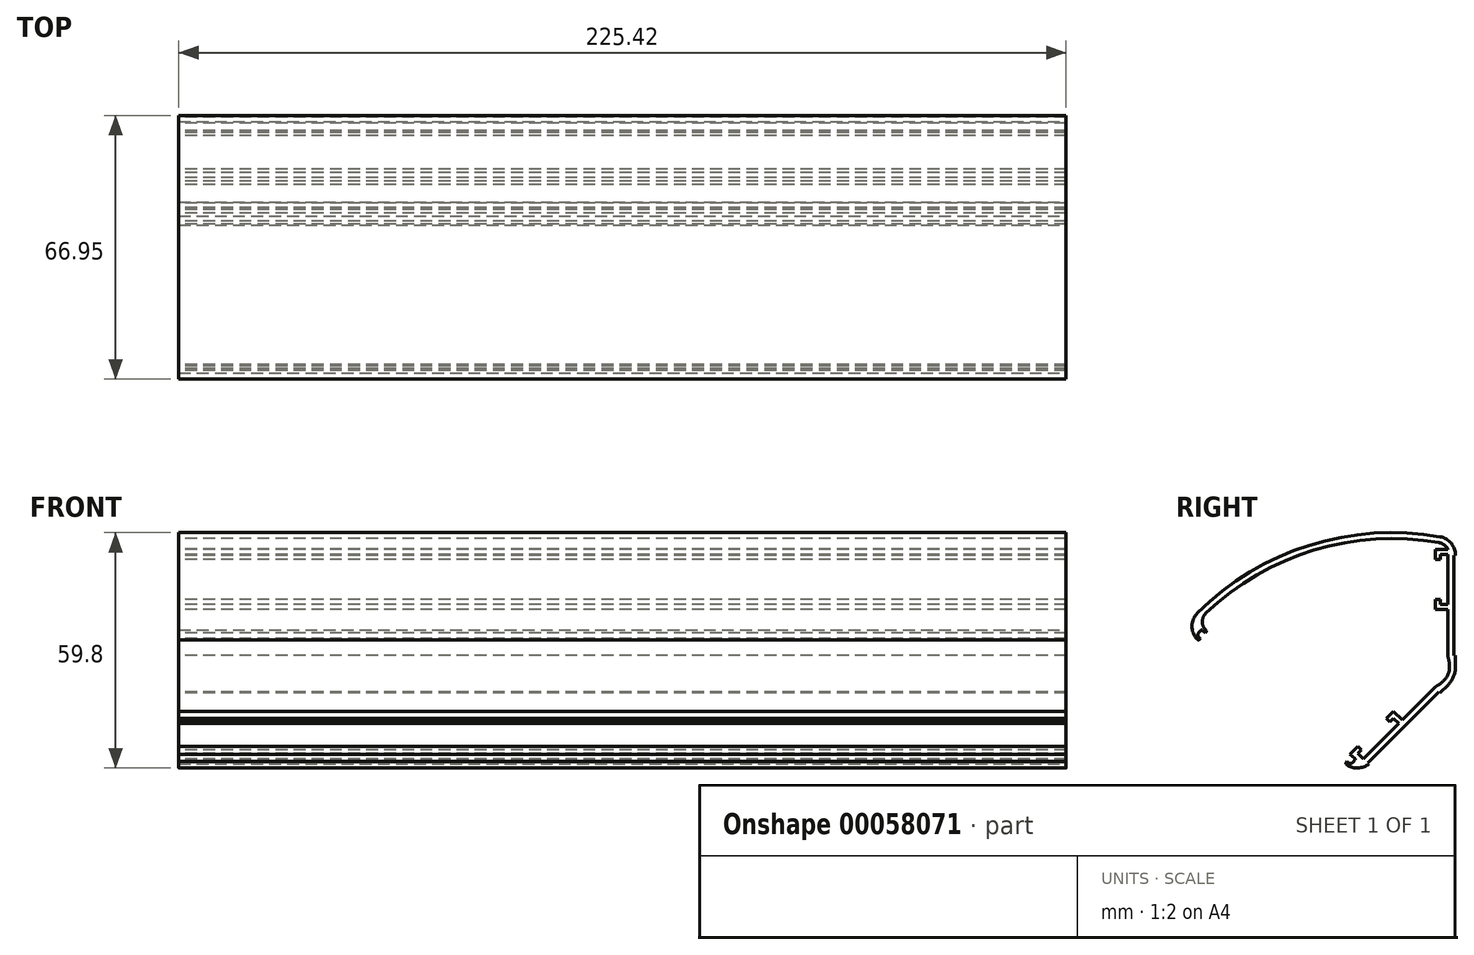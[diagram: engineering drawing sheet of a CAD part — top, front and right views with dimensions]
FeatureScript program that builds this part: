
annotation { "Feature Type Name" : "Feature", "Feature Type Description" : "" }
export const myFeature = defineFeature(function(context is Context, id is Id, definition is map)
    precondition{}
    {
        {
            var Q0;
            Q0=qCreatedBy(makeId("Right.planeOp"),FACE);
            var sketch = newSketch(context, id + "F0", { "sketchPlane" : qUnion([Q0])});
            skLineSegment(sketch, "E0", {"start": v(-24.7, -24.7) * mm, "end": v(0, 0) * mm});
            skLineSegment(sketch, "E1", {"start": v(0, 0) * mm, "end": v(0, 34.93) * mm});
            skArc(sketch, "E2", {"start": v(0, 34.93) * mm, "mid": v(-35.4, 34.1) * mm, "end": v(-65.86, 16.04) * mm});
            skLineSegment(sketch, "E3", {"start": v(-65.86, 16.04) * mm, "end": v(-69.2, 12.66) * mm});
            skLineSegment(sketch, "E4", {"start": v(-24.7, -24.7) * mm, "end": v(-69.2, 12.66) * mm});
            skLineSegment(sketch, "E5", {"start": v(-65.86, 16.04) * mm, "end": v(-24.7, -24.7) * mm, "construction": true});
            skLineSegment(sketch, "E6", {"start": v(-65.86, 16.04) * mm, "end": v(0, 34.93) * mm, "construction": true});
            skSolve(sketch);
        }
        {
            var Q0;
            Q0=qSketchRegion(id+"F0",true);
            extrude(context, id + "F1", {"entities" : qUnion([Q0]), "endBound" : BoundingType.SYMMETRIC, "depth" : 225.42 * mm});
        }
        {
            var Q0;
            Q0=makeQuery(id+"F1.opExtrude","SWEPT_EDGE",EDGE,{"disambiguationData":[OSD([sQuery(id+"F0.wireOp",EDGE,"E1"),sQuery(id+"F0.wireOp",EDGE,"E2")])]});
            var Q1;
            Q1=makeQuery(id+"F1.opExtrude","SWEPT_EDGE",EDGE,{"disambiguationData":[OSD([sQuery(id+"F0.wireOp",EDGE,"E0"),sQuery(id+"F0.wireOp",EDGE,"E4")])]});
            var Q2;
            Q2=makeQuery(id+"F1.opExtrude","SWEPT_EDGE",EDGE,{"disambiguationData":[OSD([sQuery(id+"F0.wireOp",EDGE,"E3"),sQuery(id+"F0.wireOp",EDGE,"E4")])]});
            fillet(context, id + "F2", {"entities" : qUnion([Q0, Q1, Q2]), "radius" : 4.76 * mm, "tangentPropagation" : true, "allowEdgeOverflow" : false});
        }
        {
            var Q0;
            Q0=makeQuery(id+"F1.opExtrude","SWEPT_EDGE",EDGE,{"disambiguationData":[OSD([sQuery(id+"F0.wireOp",EDGE,"E0"),sQuery(id+"F0.wireOp",EDGE,"E1")])]});
            fillet(context, id + "F3", {"entities" : qUnion([Q0]), "radius" : 6.35 * mm, "tangentPropagation" : true, "allowEdgeOverflow" : false});
        }
        {
            var Q0;
            Q0=makeQuery(id+"F1.opExtrude","CAP_FACE",FACE,{"disambiguationData":[OSD([sQuery(id+"F0.wireOp",EDGE,"E0"),sQuery(id+"F0.wireOp",EDGE,"E1"),sQuery(id+"F0.wireOp",EDGE,"E2"),sQuery(id+"F0.wireOp",EDGE,"E3"),sQuery(id+"F0.wireOp",EDGE,"E4")])],"isStart":true});
            var Q1;
            Q1=makeQuery(id+"F1.opExtrude","CAP_FACE",FACE,{"disambiguationData":[OSD([sQuery(id+"F0.wireOp",EDGE,"E0"),sQuery(id+"F0.wireOp",EDGE,"E1"),sQuery(id+"F0.wireOp",EDGE,"E2"),sQuery(id+"F0.wireOp",EDGE,"E3"),sQuery(id+"F0.wireOp",EDGE,"E4")])],"isStart":false});
            var Q2;
            Q2=makeQuery(id+"F1.opExtrude","SWEPT_FACE",FACE,{"disambiguationData":[OSD([sQuery(id+"F0.wireOp",EDGE,"E4")])]});
            shell(context, id + "F4", {"entities" : qUnion([Q0, Q1, Q2]), "thickness" : 1.52 * mm});
        }
        {
            var Q0;
            Q0=makeQuery(id+"F1.opExtrude","CAP_FACE",FACE,{"disambiguationData":[OSD([sQuery(id+"F0.wireOp",EDGE,"E0"),sQuery(id+"F0.wireOp",EDGE,"E1"),sQuery(id+"F0.wireOp",EDGE,"E2"),sQuery(id+"F0.wireOp",EDGE,"E3"),sQuery(id+"F0.wireOp",EDGE,"E4")])],"isStart":true});
            var sketch = newSketch(context, id + "F5", { "sketchPlane" : qUnion([Q0])});
            skLineSegment(sketch, "E7", {"start": v(64.27, 10.5) * mm, "end": v(63.2, 11.76) * mm});
            skArc(sketch, "E8.0", {"start": v(64.27, 10.5) * mm, "mid": v(65.42, 12.84) * mm, "end": v(64.47, 15.27) * mm});
            skArc(sketch, "E9", {"start": v(63.2, 11.76) * mm, "mid": v(64.32, 14.02) * mm, "end": v(63.37, 16.35) * mm});
            skSolve(sketch);
        }
        {
            var Q0;
            {var subQ0=sQuery(id+"F0.wireOp",EDGE,"E3");Q0=makeQuery(id+"FXWxfeTe23RxrKB_1.boolean.opBoolean","MERGE",FACE,{"derivedFrom":[makeQuery(id+"F1.opExtrude","CAP_FACE",FACE,{"disambiguationData":[OSD([sQuery(id+"F0.wireOp",EDGE,"E0"),sQuery(id+"F0.wireOp",EDGE,"E1"),sQuery(id+"F0.wireOp",EDGE,"E2"),subQ0,sQuery(id+"F0.wireOp",EDGE,"E4")])],"isStart":true}),makeQuery(id+"FXWxfeTe23RxrKB_1.opExtrude","CAP_FACE",FACE,{"disambiguationData":[OSD([subQ0,sQuery(id+"F5.wireOp",EDGE,"f8929549-29da-4568-b1ae-587f62ae2228.0"),sQuery(id+"F5.wireOp",EDGE,"E7"),sQuery(id+"F5.wireOp",EDGE,"b0cd2a88-d953-423b-8e6f-4eb86873c5e2")])],"isStart":true})]});}
            var sketch = newSketch(context, id + "F6", { "sketchPlane" : qUnion([Q0])});
            skArc(sketch, "E10.0", {"start": v(22.69, -20.53) * mm, "mid": v(24.84, -21.48) * mm, "end": v(27.06, -20.72) * mm});
            skLineSegment(sketch, "E11", {"start": v(27.06, -20.72) * mm, "end": v(26, -19.46) * mm});
            skArc(sketch, "E12", {"start": v(21.41, -19.26) * mm, "mid": v(23.67, -20.25) * mm, "end": v(26, -19.46) * mm});
            skLineSegment(sketch, "E13", {"start": v(26, -19.46) * mm, "end": v(23.84, -21.27) * mm, "construction": true});
            skSolve(sketch);
        }
        {
            var Q0;
            Q0=makeQuery(id+"F5.imprint","IMPRINT",FACE,{"disambiguationData":[TD([[makeQuery(id+"F5.imprint","IMPRINT",EDGE,{"derivedFrom":sQuery(id+"F5.wireOp",EDGE,"E7")}),-1.0]])]});
            var Q1;
            {var subQ0=sQuery(id+"F6.wireOp",EDGE,"E10.0");Q1=makeQuery(id+"F6.imprint","IMPRINT",FACE,{"disambiguationData":[TD([[makeQuery(id+"F6.imprint","IMPRINT",EDGE,{"derivedFrom":subQ0}),1.0]])]});}
            var Q2;
            Q2=makeQuery(id+"F1.opExtrude","CAP_FACE",FACE,{"disambiguationData":[OSD([sQuery(id+"F0.wireOp",EDGE,"E0"),sQuery(id+"F0.wireOp",EDGE,"E1"),sQuery(id+"F0.wireOp",EDGE,"E2"),sQuery(id+"F0.wireOp",EDGE,"E3"),sQuery(id+"F0.wireOp",EDGE,"E4")])],"isStart":false});
            extrude(context, id + "F7", {"entities" : qUnion([Q0, Q1]), "operationType" : NewBodyOperationType.ADD, "endBound" : BoundingType.UP_TO_SURFACE, "oppositeDirection" : true, "endBoundEntityFace" : qUnion([Q2]), "depth" : 25.4 * mm});
        }
        {
            var Q0;
            {var subQ0=sQuery(id+"F0.wireOp",EDGE,"E0");var subQ1=sQuery(id+"F0.wireOp",EDGE,"E2");Q0=makeQuery(id+"F7.boolean.opBoolean","MERGE",FACE,{"derivedFrom":[makeQuery(id+"F1.opExtrude","CAP_FACE",FACE,{"disambiguationData":[OSD([subQ0,sQuery(id+"F0.wireOp",EDGE,"E1"),subQ1,sQuery(id+"F0.wireOp",EDGE,"E3"),sQuery(id+"F0.wireOp",EDGE,"E4")])],"isStart":true}),makeQuery(id+"F7.opExtrude","CAP_FACE",FACE,{"disambiguationData":[OSD([subQ1,sQuery(id+"F5.wireOp",EDGE,"E7"),sQuery(id+"F5.wireOp",EDGE,"E8.0"),sQuery(id+"F5.wireOp",EDGE,"E9")])],"isStart":true}),makeQuery(id+"F7.opExtrude","CAP_FACE",FACE,{"disambiguationData":[OSD([subQ0,sQuery(id+"F6.wireOp",EDGE,"E10.0"),sQuery(id+"F6.wireOp",EDGE,"E11"),sQuery(id+"F6.wireOp",EDGE,"E12")])],"isStart":true})]});}
            var sketch = newSketch(context, id + "F8", { "sketchPlane" : qUnion([Q0])});
            skLineSegment(sketch, "E14", {"start": v(64.19, 10.6) * mm, "end": v(26.98, -20.63) * mm, "construction": true});
            skSolve(sketch);
        }
        {
            var Q0;
            {var subQ4=sQuery(id+"F0.wireOp",EDGE,"E0");var subQ12=makeQuery(id+"F1.opExtrude","CAP_EDGE",EDGE,{"disambiguationData":[OSD([subQ4])],"isStart":true});Q0=makeQuery(id+"F8.imprint","IMPRINT",FACE,{"disambiguationData":[TD([[makeQuery(id+"F8.imprint","IMPRINT",EDGE,{"derivedFrom":subQ12}),-1.0]])]});}
            var sketch = newSketch(context, id + "F9", { "sketchPlane" : qUnion([Q0])});
            skLineSegment(sketch, "E15", {"start": v(63.57, 11.33) * mm, "end": v(64.8, 9.87) * mm});
            skLineSegment(sketch, "E16", {"start": v(64.8, 9.87) * mm, "end": v(65.77, 10.68) * mm});
            skLineSegment(sketch, "E17", {"start": v(65.77, 10.68) * mm, "end": v(64.55, 12.14) * mm});
            skLineSegment(sketch, "E18", {"start": v(64.55, 12.14) * mm, "end": v(63.57, 11.33) * mm});
            skPoint(sketch, "E19", {"position": v(64.19, 10.6) * mm});
            skSolve(sketch);
        }
        {
            var Q0;
            {var subQ4=sQuery(id+"F0.wireOp",EDGE,"E0");var subQ12=makeQuery(id+"F1.opExtrude","CAP_EDGE",EDGE,{"disambiguationData":[OSD([subQ4])],"isStart":true});Q0=makeQuery(id+"F8.imprint","IMPRINT",FACE,{"disambiguationData":[TD([[makeQuery(id+"F8.imprint","IMPRINT",EDGE,{"derivedFrom":subQ12}),-1.0]])]});}
            var sketch = newSketch(context, id + "F10", { "sketchPlane" : qUnion([Q0])});
            skLineSegment(sketch, "E20", {"start": v(26.37, -19.9) * mm, "end": v(27.59, -21.36) * mm});
            skLineSegment(sketch, "E21", {"start": v(27.59, -21.36) * mm, "end": v(26.62, -22.17) * mm});
            skLineSegment(sketch, "E22", {"start": v(26.62, -22.17) * mm, "end": v(25.4, -20.71) * mm});
            skLineSegment(sketch, "E23", {"start": v(25.4, -20.71) * mm, "end": v(26.37, -19.9) * mm});
            skPoint(sketch, "E24", {"position": v(26.98, -20.63) * mm});
            skSolve(sketch);
        }
        {
            var Q0;
            Q0=qSketchRegion(id+"F9",true);
            var Q1;
            Q1=qSketchRegion(id+"F10",true);
            var Q2;
            {var subQ0=sQuery(id+"F0.wireOp",EDGE,"E0");var subQ1=sQuery(id+"F0.wireOp",EDGE,"E2");Q2=makeQuery(id+"F7.boolean.opBoolean","MERGE",FACE,{"derivedFrom":[makeQuery(id+"F1.opExtrude","CAP_FACE",FACE,{"disambiguationData":[OSD([subQ0,sQuery(id+"F0.wireOp",EDGE,"E1"),subQ1,sQuery(id+"F0.wireOp",EDGE,"E3"),sQuery(id+"F0.wireOp",EDGE,"E4")])],"isStart":false}),makeQuery(id+"F7.opExtrude","CAP_FACE",FACE,{"disambiguationData":[OSD([subQ1,sQuery(id+"F5.wireOp",EDGE,"E7"),sQuery(id+"F5.wireOp",EDGE,"E8.0"),sQuery(id+"F5.wireOp",EDGE,"E9")])],"isStart":false}),makeQuery(id+"F7.opExtrude","CAP_FACE",FACE,{"disambiguationData":[OSD([subQ0,sQuery(id+"F6.wireOp",EDGE,"E10.0"),sQuery(id+"F6.wireOp",EDGE,"E11"),sQuery(id+"F6.wireOp",EDGE,"E12")])],"isStart":false})]});}
            extrude(context, id + "F11", {"entities" : qUnion([Q0, Q1]), "operationType" : NewBodyOperationType.REMOVE, "endBound" : BoundingType.UP_TO_SURFACE, "oppositeDirection" : true, "endBoundEntityFace" : qUnion([Q2]), "depth" : 25.4 * mm});
        }
        {
            var Q0;
            Q0=makeQuery(id+"F11.boolean.opBoolean","COPY",EDGE,{"derivedFrom":makeQuery(id+"F11.opExtrude","SWEPT_EDGE",EDGE,{"disambiguationData":[OSD([sQuery(id+"F10.wireOp",EDGE,"E21"),sQuery(id+"F10.wireOp",EDGE,"E22")])]})});
            var Q1;
            Q1=makeQuery(id+"F11.boolean.opBoolean","COPY",EDGE,{"derivedFrom":makeQuery(id+"F11.opExtrude","SWEPT_EDGE",EDGE,{"disambiguationData":[OSD([sQuery(id+"F9.wireOp",EDGE,"E16"),sQuery(id+"F9.wireOp",EDGE,"E17")])]})});
            fillet(context, id + "F12", {"entities" : qUnion([Q0, Q1]), "radius" : 0.76 * mm, "tangentPropagation" : true, "allowEdgeOverflow" : false});
        }
        {
            var Q0;
            {var subQ0=sQuery(id+"F0.wireOp",EDGE,"E4");Q0=makeQuery(id+"F2.opFillet","BLEND_EDGE",EDGE,{"blendedFrom":[makeQuery(id+"F1.opExtrude","SWEPT_EDGE",EDGE,{"disambiguationData":[OSD([sQuery(id+"F0.wireOp",EDGE,"E3"),subQ0])]}),makeQuery(id+"F1.opExtrude","SWEPT_FACE",FACE,{"disambiguationData":[OSD([subQ0])]})],"blendedInto":[makeQuery(id+"F1.opExtrude","SWEPT_FACE",FACE,{"disambiguationData":[OSD([subQ0])]})]});}
            var Q1;
            {var subQ0=sQuery(id+"F0.wireOp",EDGE,"E4");Q1=makeQuery(id+"F2.opFillet","BLEND_EDGE",EDGE,{"blendedFrom":[makeQuery(id+"F1.opExtrude","SWEPT_EDGE",EDGE,{"disambiguationData":[OSD([sQuery(id+"F0.wireOp",EDGE,"E0"),subQ0])]}),makeQuery(id+"F1.opExtrude","SWEPT_FACE",FACE,{"disambiguationData":[OSD([subQ0])]})],"blendedInto":[makeQuery(id+"F1.opExtrude","SWEPT_FACE",FACE,{"disambiguationData":[OSD([subQ0])]})]});}
            fillet(context, id + "F13", {"entities" : qUnion([Q0, Q1]), "radius" : 0.5 * mm, "tangentPropagation" : true, "allowEdgeOverflow" : false});
        }
        {
            var Q0;
            Q0=makeQuery(id+"F11.boolean.opBoolean","COPY",EDGE,{"derivedFrom":makeQuery(id+"F11.opExtrude","SWEPT_EDGE",EDGE,{"disambiguationData":[OSD([sQuery(id+"F10.wireOp",EDGE,"E22"),sQuery(id+"F10.wireOp",EDGE,"E23")])]})});
            var Q1;
            Q1=makeQuery(id+"F11.boolean.opBoolean","COPY",EDGE,{"derivedFrom":makeQuery(id+"F11.opExtrude","SWEPT_EDGE",EDGE,{"disambiguationData":[OSD([sQuery(id+"F0.wireOp",EDGE,"E0"),sQuery(id+"F0.wireOp",EDGE,"E1"),sQuery(id+"F0.wireOp",EDGE,"E2"),sQuery(id+"F0.wireOp",EDGE,"E3"),sQuery(id+"F0.wireOp",EDGE,"E4"),sQuery(id+"F6.wireOp",EDGE,"E11"),sQuery(id+"F10.wireOp",EDGE,"E20"),sQuery(id+"F10.wireOp",EDGE,"E23")])]})});
            var Q2;
            Q2=makeQuery(id+"F7.opExtrude","SWEPT_EDGE",EDGE,{"disambiguationData":[OSD([sQuery(id+"F6.wireOp",EDGE,"E11"),sQuery(id+"F6.wireOp",EDGE,"E12")])]});
            var Q3;
            Q3=makeQuery(id+"F11.boolean.opBoolean","COPY",EDGE,{"derivedFrom":makeQuery(id+"F11.opExtrude","SWEPT_EDGE",EDGE,{"disambiguationData":[OSD([sQuery(id+"F0.wireOp",EDGE,"E0"),sQuery(id+"F0.wireOp",EDGE,"E1"),sQuery(id+"F0.wireOp",EDGE,"E2"),sQuery(id+"F0.wireOp",EDGE,"E3"),sQuery(id+"F0.wireOp",EDGE,"E4"),sQuery(id+"F5.wireOp",EDGE,"E7"),sQuery(id+"F9.wireOp",EDGE,"E15"),sQuery(id+"F9.wireOp",EDGE,"E18")])]})});
            var Q4;
            Q4=makeQuery(id+"F7.opExtrude","SWEPT_EDGE",EDGE,{"disambiguationData":[OSD([sQuery(id+"F5.wireOp",EDGE,"E7"),sQuery(id+"F5.wireOp",EDGE,"E9")])]});
            var Q5;
            Q5=makeQuery(id+"F11.boolean.opBoolean","COPY",EDGE,{"derivedFrom":makeQuery(id+"F11.opExtrude","SWEPT_EDGE",EDGE,{"disambiguationData":[OSD([sQuery(id+"F9.wireOp",EDGE,"E17"),sQuery(id+"F9.wireOp",EDGE,"E18")])]})});
            fillet(context, id + "F14", {"entities" : qUnion([Q0, Q1, Q2, Q3, Q4, Q5]), "radius" : 0.25 * mm, "tangentPropagation" : true, "allowEdgeOverflow" : false});
        }
        {
            var Q0;
            {var subQ2=sQuery(id+"F0.wireOp",EDGE,"E2");var subQ10=makeQuery(id+"F1.opExtrude","CAP_EDGE",EDGE,{"disambiguationData":[OSD([subQ2])],"isStart":true});Q0=makeQuery(id+"F8.imprint","IMPRINT",FACE,{"disambiguationData":[TD([[makeQuery(id+"F8.imprint","IMPRINT",EDGE,{"derivedFrom":subQ10}),-1.0]])]});}
            var sketch = newSketch(context, id + "F15", { "sketchPlane" : qUnion([Q0])});
            skLineSegment(sketch, "E25.0", {"start": v(0, 0) * mm, "end": v(0, 31.05) * mm, "construction": true});
            skLineSegment(sketch, "E25.1", {"start": v(21.6, -21.6) * mm, "end": v(0, 0) * mm, "construction": true});
            skLineSegment(sketch, "E26", {"start": v(0, 0) * mm, "end": v(1.9, 0.78) * mm, "construction": true});
            skSolve(sketch);
        }
        {
            var Q0;
            {var subQ2=sQuery(id+"F0.wireOp",EDGE,"E2");var subQ10=makeQuery(id+"F1.opExtrude","CAP_EDGE",EDGE,{"disambiguationData":[OSD([subQ2])],"isStart":true});Q0=makeQuery(id+"F8.imprint","IMPRINT",FACE,{"disambiguationData":[TD([[makeQuery(id+"F8.imprint","IMPRINT",EDGE,{"derivedFrom":subQ10}),-1.0]])]});}
            var sketch = newSketch(context, id + "F16", { "sketchPlane" : qUnion([Q0])});
            skLineSegment(sketch, "E27.bottom", {"start": v(0, 31.05) * mm, "end": v(0.4, 31.05) * mm});
            skLineSegment(sketch, "E27.top", {"start": v(0, 5.65) * mm, "end": v(0.4, 5.65) * mm});
            skLineSegment(sketch, "E27.left", {"start": v(0, 31.05) * mm, "end": v(0, 5.65) * mm});
            skLineSegment(sketch, "E27.right", {"start": v(0.4, 31.05) * mm, "end": v(0.4, 5.65) * mm});
            skLineSegment(sketch, "E28.MirrorCS", {"start": v(4, -4) * mm, "end": v(4.27, -3.71) * mm});
            skLineSegment(sketch, "E29.MirrorCS", {"start": v(22.23, -21.67) * mm, "end": v(4.27, -3.71) * mm});
            skLineSegment(sketch, "E30.MirrorCS", {"start": v(21.95, -21.95) * mm, "end": v(4, -4) * mm});
            skLineSegment(sketch, "E31.MirrorCS", {"start": v(21.95, -21.95) * mm, "end": v(22.23, -21.67) * mm});
            skSolve(sketch);
        }
        {
            var Q0;
            Q0=qSketchRegion(id+"F16",true);
            var Q1;
            {var subQ0=sQuery(id+"F0.wireOp",EDGE,"E0");var subQ1=sQuery(id+"F0.wireOp",EDGE,"E2");Q1=makeQuery(id+"F7.boolean.opBoolean","MERGE",FACE,{"derivedFrom":[makeQuery(id+"F1.opExtrude","CAP_FACE",FACE,{"disambiguationData":[OSD([subQ0,sQuery(id+"F0.wireOp",EDGE,"E1"),subQ1,sQuery(id+"F0.wireOp",EDGE,"E3"),sQuery(id+"F0.wireOp",EDGE,"E4")])],"isStart":false}),makeQuery(id+"F7.opExtrude","CAP_FACE",FACE,{"disambiguationData":[OSD([subQ1,sQuery(id+"F5.wireOp",EDGE,"E7"),sQuery(id+"F5.wireOp",EDGE,"E8.0"),sQuery(id+"F5.wireOp",EDGE,"E9")])],"isStart":false}),makeQuery(id+"F7.opExtrude","CAP_FACE",FACE,{"disambiguationData":[OSD([subQ0,sQuery(id+"F6.wireOp",EDGE,"E10.0"),sQuery(id+"F6.wireOp",EDGE,"E11"),sQuery(id+"F6.wireOp",EDGE,"E12")])],"isStart":false})]});}
            extrude(context, id + "F17", {"entities" : qUnion([Q0]), "operationType" : NewBodyOperationType.REMOVE, "endBound" : BoundingType.UP_TO_SURFACE, "oppositeDirection" : true, "endBoundEntityFace" : qUnion([Q1]), "depth" : 25.4 * mm});
        }
        {
            var Q0;
            {var subQ2=sQuery(id+"F0.wireOp",EDGE,"E2");var subQ10=makeQuery(id+"F1.opExtrude","CAP_EDGE",EDGE,{"disambiguationData":[OSD([subQ2])],"isStart":true});Q0=makeQuery(id+"F8.imprint","IMPRINT",FACE,{"disambiguationData":[TD([[makeQuery(id+"F8.imprint","IMPRINT",EDGE,{"derivedFrom":subQ10}),-1.0]])]});}
            var sketch = newSketch(context, id + "F18", { "sketchPlane" : qUnion([Q0])});
            skLineSegment(sketch, "E32.left", {"start": v(1.52, 31.05) * mm, "end": v(1.52, 2.63) * mm});
            skLineSegment(sketch, "E32.right", {"start": v(1.92, 32.6) * mm, "end": v(1.92, 5.65) * mm});
            skArc(sketch, "E33", {"start": v(1.52, 31.05) * mm, "mid": v(1.62, 31.85) * mm, "end": v(1.92, 32.6) * mm});
            skArc(sketch, "E34", {"start": v(1.92, 5.65) * mm, "mid": v(1.9, 5.25) * mm, "end": v(1.82, 4.85) * mm});
            skArc(sketch, "E35", {"start": v(1.82, 4.85) * mm, "mid": v(1.6, 3.75) * mm, "end": v(1.52, 2.63) * mm});
            skLineSegment(sketch, "E36.MirrorCS", {"start": v(24.4, -21.7) * mm, "end": v(5.35, -2.63) * mm});
            skLineSegment(sketch, "E37.MirrorCS", {"start": v(23.03, -20.88) * mm, "end": v(2.94, -0.78) * mm});
            skArc(sketch, "E38.MirrorCS", {"start": v(4.72, -2.15) * mm, "mid": v(3.78, -1.52) * mm, "end": v(2.94, -0.78) * mm});
            skArc(sketch, "E39.MirrorCS", {"start": v(5.35, -2.63) * mm, "mid": v(5.05, -2.37) * mm, "end": v(4.72, -2.15) * mm});
            skArc(sketch, "E40.MirrorCS", {"start": v(23.03, -20.88) * mm, "mid": v(23.67, -21.37) * mm, "end": v(24.4, -21.7) * mm});
            skSolve(sketch);
        }
        {
            var Q0;
            Q0=qSketchRegion(id+"F18",true);
            var Q1;
            {var subQ0=sQuery(id+"F0.wireOp",EDGE,"E0");var subQ1=sQuery(id+"F0.wireOp",EDGE,"E2");Q1=makeQuery(id+"F7.boolean.opBoolean","MERGE",FACE,{"derivedFrom":[makeQuery(id+"F1.opExtrude","CAP_FACE",FACE,{"disambiguationData":[OSD([subQ0,sQuery(id+"F0.wireOp",EDGE,"E1"),subQ1,sQuery(id+"F0.wireOp",EDGE,"E3"),sQuery(id+"F0.wireOp",EDGE,"E4")])],"isStart":false}),makeQuery(id+"F7.opExtrude","CAP_FACE",FACE,{"disambiguationData":[OSD([subQ1,sQuery(id+"F5.wireOp",EDGE,"E7"),sQuery(id+"F5.wireOp",EDGE,"E8.0"),sQuery(id+"F5.wireOp",EDGE,"E9")])],"isStart":false}),makeQuery(id+"F7.opExtrude","CAP_FACE",FACE,{"disambiguationData":[OSD([subQ0,sQuery(id+"F6.wireOp",EDGE,"E10.0"),sQuery(id+"F6.wireOp",EDGE,"E11"),sQuery(id+"F6.wireOp",EDGE,"E12")])],"isStart":false})]});}
            extrude(context, id + "F19", {"entities" : qUnion([Q0]), "operationType" : NewBodyOperationType.ADD, "endBound" : BoundingType.UP_TO_SURFACE, "oppositeDirection" : true, "endBoundEntityFace" : qUnion([Q1]), "depth" : 25.4 * mm});
        }
        {
            var Q0;
            {var subQ2=sQuery(id+"F0.wireOp",EDGE,"E2");var subQ10=makeQuery(id+"F1.opExtrude","CAP_EDGE",EDGE,{"disambiguationData":[OSD([subQ2])],"isStart":true});Q0=makeQuery(id+"F8.imprint","IMPRINT",FACE,{"disambiguationData":[TD([[makeQuery(id+"F8.imprint","IMPRINT",EDGE,{"derivedFrom":subQ10}),-1.0]])]});}
            var sketch = newSketch(context, id + "F20", { "sketchPlane" : qUnion([Q0])});
            skLineSegment(sketch, "E41", {"start": v(13.55, -10.83) * mm, "end": v(15.8, -8.59) * mm});
            skLineSegment(sketch, "E42", {"start": v(17.59, -10.38) * mm, "end": v(15.8, -8.59) * mm});
            skLineSegment(sketch, "E43", {"start": v(17.59, -10.38) * mm, "end": v(16.7, -11.28) * mm});
            skLineSegment(sketch, "E44", {"start": v(15.8, -10.38) * mm, "end": v(16.7, -11.28) * mm});
            skLineSegment(sketch, "E45", {"start": v(15.8, -10.38) * mm, "end": v(14.45, -11.73) * mm});
            skLineSegment(sketch, "E46", {"start": v(13.55, -10.83) * mm, "end": v(14.45, -11.73) * mm});
            skLineSegment(sketch, "E47", {"start": v(24.77, -17.57) * mm, "end": v(26.77, -19.56) * mm});
            skLineSegment(sketch, "E48", {"start": v(26.77, -19.56) * mm, "end": v(24.32, -21.6) * mm});
            skLineSegment(sketch, "E49", {"start": v(24.32, -21.6) * mm, "end": v(23.43, -20.71) * mm});
            skLineSegment(sketch, "E50", {"start": v(24.77, -17.57) * mm, "end": v(23.88, -18.47) * mm});
            skLineSegment(sketch, "E51", {"start": v(23.88, -18.47) * mm, "end": v(24.77, -19.36) * mm});
            skLineSegment(sketch, "E52", {"start": v(24.77, -19.36) * mm, "end": v(23.43, -20.71) * mm});
            skLineSegment(sketch, "E53.MirrorCS", {"start": v(1.92, 17.24) * mm, "end": v(1.92, 18.5) * mm});
            skLineSegment(sketch, "E54.MirrorCS", {"start": v(1.92, 17.24) * mm, "end": v(5.1, 17.24) * mm});
            skLineSegment(sketch, "E55.MirrorCS", {"start": v(3.83, 18.5) * mm, "end": v(1.92, 18.5) * mm});
            skLineSegment(sketch, "E56.MirrorCS", {"start": v(3.83, 18.5) * mm, "end": v(3.83, 19.78) * mm});
            skLineSegment(sketch, "E57.MirrorCS", {"start": v(5.1, 19.78) * mm, "end": v(3.83, 19.78) * mm});
            skLineSegment(sketch, "E58.MirrorCS", {"start": v(5.1, 19.78) * mm, "end": v(5.1, 17.24) * mm});
            skLineSegment(sketch, "E59.MirrorCS", {"start": v(3.83, 31.2) * mm, "end": v(1.92, 31.2) * mm});
            skLineSegment(sketch, "E60.MirrorCS", {"start": v(3.83, 29.94) * mm, "end": v(3.83, 31.2) * mm});
            skLineSegment(sketch, "E61.MirrorCS", {"start": v(5.1, 29.94) * mm, "end": v(3.83, 29.94) * mm});
            skLineSegment(sketch, "E62.MirrorCS", {"start": v(5.1, 29.94) * mm, "end": v(5.1, 32.76) * mm});
            skLineSegment(sketch, "E63.MirrorCS", {"start": v(5.1, 32.76) * mm, "end": v(1.92, 32.48) * mm});
            skLineSegment(sketch, "E64.MirrorCS", {"start": v(1.92, 32.48) * mm, "end": v(1.92, 31.2) * mm});
            skSolve(sketch);
        }
        {
            var Q0;
            Q0 = qSketchRegion(id + "F20", true);
            var Q1;
            {var subQ0=sQuery(id+"F0.wireOp",EDGE,"E0");var subQ1=sQuery(id+"F0.wireOp",EDGE,"E2");Q1=makeQuery(id+"F19.boolean.opBoolean","MERGE",FACE,{"derivedFrom":[makeQuery(id+"F7.boolean.opBoolean","MERGE",FACE,{"derivedFrom":[makeQuery(id+"F1.opExtrude","CAP_FACE",FACE,{"disambiguationData":[OSD([subQ0,sQuery(id+"F0.wireOp",EDGE,"E1"),subQ1,sQuery(id+"F0.wireOp",EDGE,"E3"),sQuery(id+"F0.wireOp",EDGE,"E4")])],"isStart":false}),makeQuery(id+"F7.opExtrude","CAP_FACE",FACE,{"disambiguationData":[OSD([subQ1,sQuery(id+"F5.wireOp",EDGE,"E7"),sQuery(id+"F5.wireOp",EDGE,"E8.0"),sQuery(id+"F5.wireOp",EDGE,"E9")])],"isStart":false}),makeQuery(id+"F7.opExtrude","CAP_FACE",FACE,{"disambiguationData":[OSD([subQ0,sQuery(id+"F6.wireOp",EDGE,"E10.0"),sQuery(id+"F6.wireOp",EDGE,"E11"),sQuery(id+"F6.wireOp",EDGE,"E12")])],"isStart":false})]}),makeQuery(id+"F19.opExtrude","CAP_FACE",FACE,{"disambiguationData":[OSD([sQuery(id+"F18.wireOp",EDGE,"E32.left"),sQuery(id+"F18.wireOp",EDGE,"E32.right"),sQuery(id+"F18.wireOp",EDGE,"cf68511a-fb8e-4c82-880c-a71a2c55e88e"),sQuery(id+"F18.wireOp",EDGE,"bed6c8f6-f93f-4cf1-8f14-03c9fbdcd656"),sQuery(id+"F18.wireOp",EDGE,"E33"),sQuery(id+"F18.wireOp",EDGE,"6943048b-c902-4e26-99fd-97bb197fedb8"),sQuery(id+"F18.wireOp",EDGE,"E34"),sQuery(id+"F18.wireOp",EDGE,"E35")])],"isStart":false}),makeQuery(id+"F19.opExtrude","CAP_FACE",FACE,{"disambiguationData":[OSD([sQuery(id+"F18.wireOp",EDGE,"6b1a1502-6643-4882-9dfe-d4cd869500f90.MirrorCS"),sQuery(id+"F18.wireOp",EDGE,"c14309ee-7e91-464b-9b86-53066cb974710.MirrorCS"),sQuery(id+"F18.wireOp",EDGE,"c51dd276-225b-4767-8180-87f40df51ec00.MirrorCS"),sQuery(id+"F18.wireOp",EDGE,"bbbe13b7-8c27-4469-9673-4603b33e01e60.MirrorCS"),sQuery(id+"F18.wireOp",EDGE,"80786fb8-0e63-45c2-85fc-b14a924401060.MirrorCS"),sQuery(id+"F18.wireOp",EDGE,"a4a722fd-dec7-4de3-b669-0f050d30c4590.MirrorCS"),sQuery(id+"F18.wireOp",EDGE,"de32fec8-abd8-49ad-a09a-0bd41e20e6420.MirrorCS"),sQuery(id+"F18.wireOp",EDGE,"e39107af-05ad-48be-bcdf-b232e91616470.MirrorCS")])],"isStart":false})]});}
            extrude(context, id + "F21", {"entities" : qUnion([Q0]), "operationType" : NewBodyOperationType.ADD, "endBound" : BoundingType.UP_TO_SURFACE, "oppositeDirection" : true, "endBoundEntityFace" : qUnion([Q1]), "depth" : 25.4 * mm});
        }
        {
            var Q0;
            {var subQ0=sQuery(id+"F0.wireOp",EDGE,"E0");var subQ1=sQuery(id+"F0.wireOp",EDGE,"E2");Q0=makeQuery(id+"F21.boolean.opBoolean","MERGE",FACE,{"derivedFrom":[makeQuery(id+"F19.boolean.opBoolean","MERGE",FACE,{"derivedFrom":[makeQuery(id+"F7.boolean.opBoolean","MERGE",FACE,{"derivedFrom":[makeQuery(id+"F1.opExtrude","CAP_FACE",FACE,{"disambiguationData":[OSD([subQ0,sQuery(id+"F0.wireOp",EDGE,"E1"),subQ1,sQuery(id+"F0.wireOp",EDGE,"E3"),sQuery(id+"F0.wireOp",EDGE,"E4")])],"isStart":true}),makeQuery(id+"F7.opExtrude","CAP_FACE",FACE,{"disambiguationData":[OSD([subQ1,sQuery(id+"F5.wireOp",EDGE,"E7"),sQuery(id+"F5.wireOp",EDGE,"E8.0"),sQuery(id+"F5.wireOp",EDGE,"E9")])],"isStart":true}),makeQuery(id+"F7.opExtrude","CAP_FACE",FACE,{"disambiguationData":[OSD([subQ0,sQuery(id+"F6.wireOp",EDGE,"E10.0"),sQuery(id+"F6.wireOp",EDGE,"E11"),sQuery(id+"F6.wireOp",EDGE,"E12")])],"isStart":true})]}),makeQuery(id+"F19.opExtrude","CAP_FACE",FACE,{"disambiguationData":[OSD([sQuery(id+"F18.wireOp",EDGE,"E32.left"),sQuery(id+"F18.wireOp",EDGE,"E32.right"),sQuery(id+"F18.wireOp",EDGE,"E33"),sQuery(id+"F18.wireOp",EDGE,"6943048b-c902-4e26-99fd-97bb197fedb8"),sQuery(id+"F18.wireOp",EDGE,"E34"),sQuery(id+"F18.wireOp",EDGE,"E35")])],"isStart":true}),makeQuery(id+"F19.opExtrude","CAP_FACE",FACE,{"disambiguationData":[OSD([sQuery(id+"F18.wireOp",EDGE,"6df5da01-636c-4fa1-a154-6959b493e0280.MirrorCS"),sQuery(id+"F18.wireOp",EDGE,"8fe4f21a-40d9-4eee-a692-7fc8709130e30.MirrorCS"),sQuery(id+"F18.wireOp",EDGE,"7f15d878-ce14-4078-be7b-5ededd66effc0.MirrorCS"),sQuery(id+"F18.wireOp",EDGE,"1ae5cb18-7ae8-489c-8bf4-f5e9a86dfa970.MirrorCS"),sQuery(id+"F18.wireOp",EDGE,"720fc289-6002-463f-9985-f6a57c39472f0.MirrorCS"),sQuery(id+"F18.wireOp",EDGE,"14feacf6-0e8a-4ab1-8ffb-d78e7fce1ae00.MirrorCS")])],"isStart":true})]}),makeQuery(id+"F21.opExtrude","CAP_FACE",FACE,{"disambiguationData":[OSD([sQuery(id+"F20.wireOp",EDGE,"E41"),sQuery(id+"F20.wireOp",EDGE,"E42"),sQuery(id+"F20.wireOp",EDGE,"E43"),sQuery(id+"F20.wireOp",EDGE,"E44"),sQuery(id+"F20.wireOp",EDGE,"E45"),sQuery(id+"F20.wireOp",EDGE,"E46")])],"isStart":true}),makeQuery(id+"F21.opExtrude","CAP_FACE",FACE,{"disambiguationData":[OSD([sQuery(id+"F20.wireOp",EDGE,"E47"),sQuery(id+"F20.wireOp",EDGE,"E48"),sQuery(id+"F20.wireOp",EDGE,"E49"),sQuery(id+"F20.wireOp",EDGE,"E50"),sQuery(id+"F20.wireOp",EDGE,"E51"),sQuery(id+"F20.wireOp",EDGE,"E52")])],"isStart":true}),makeQuery(id+"F21.opExtrude","CAP_FACE",FACE,{"disambiguationData":[OSD([sQuery(id+"F20.wireOp",EDGE,"E53.MirrorCS"),sQuery(id+"F20.wireOp",EDGE,"E54.MirrorCS"),sQuery(id+"F20.wireOp",EDGE,"E55.MirrorCS"),sQuery(id+"F20.wireOp",EDGE,"E56.MirrorCS"),sQuery(id+"F20.wireOp",EDGE,"E57.MirrorCS"),sQuery(id+"F20.wireOp",EDGE,"E58.MirrorCS")])],"isStart":true}),makeQuery(id+"F21.opExtrude","CAP_FACE",FACE,{"disambiguationData":[OSD([sQuery(id+"F20.wireOp",EDGE,"E59.MirrorCS"),sQuery(id+"F20.wireOp",EDGE,"E60.MirrorCS"),sQuery(id+"F20.wireOp",EDGE,"E61.MirrorCS"),sQuery(id+"F20.wireOp",EDGE,"E62.MirrorCS"),sQuery(id+"F20.wireOp",EDGE,"E63.MirrorCS"),sQuery(id+"F20.wireOp",EDGE,"E64.MirrorCS")])],"isStart":true})]});}
            var sketch = newSketch(context, id + "F22", { "sketchPlane" : qUnion([Q0])});
            skLineSegment(sketch, "E65", {"start": v(1.92, 32.48) * mm, "end": v(5.1, 32.48) * mm});
            skLineSegment(sketch, "E66", {"start": v(5.1, 32.48) * mm, "end": v(5.1, 32.76) * mm});
            skLineSegment(sketch, "E67", {"start": v(1.92, 32.48) * mm, "end": v(5.1, 32.76) * mm});
            skLineSegment(sketch, "E68", {"start": v(23.88, -18.47) * mm, "end": v(24.77, -19.36) * mm});
            skLineSegment(sketch, "E69", {"start": v(24.77, -19.36) * mm, "end": v(23.43, -20.71) * mm});
            skLineSegment(sketch, "E70", {"start": v(23.43, -20.71) * mm, "end": v(22.53, -19.81) * mm});
            skLineSegment(sketch, "E71", {"start": v(22.53, -19.81) * mm, "end": v(23.88, -18.47) * mm});
            skSolve(sketch);
        }
        {
            var Q0;
            Q0 = qSketchRegion(id + "F22", true);
            var Q1;
            {var subQ0=sQuery(id+"F0.wireOp",EDGE,"E0");var subQ1=sQuery(id+"F0.wireOp",EDGE,"E2");Q1=makeQuery(id+"F21.boolean.opBoolean","MERGE",FACE,{"derivedFrom":[makeQuery(id+"F19.boolean.opBoolean","MERGE",FACE,{"derivedFrom":[makeQuery(id+"F7.boolean.opBoolean","MERGE",FACE,{"derivedFrom":[makeQuery(id+"F1.opExtrude","CAP_FACE",FACE,{"disambiguationData":[OSD([subQ0,sQuery(id+"F0.wireOp",EDGE,"E1"),subQ1,sQuery(id+"F0.wireOp",EDGE,"E3"),sQuery(id+"F0.wireOp",EDGE,"E4")])],"isStart":false}),makeQuery(id+"F7.opExtrude","CAP_FACE",FACE,{"disambiguationData":[OSD([subQ1,sQuery(id+"F5.wireOp",EDGE,"E7"),sQuery(id+"F5.wireOp",EDGE,"E8.0"),sQuery(id+"F5.wireOp",EDGE,"E9")])],"isStart":false}),makeQuery(id+"F7.opExtrude","CAP_FACE",FACE,{"disambiguationData":[OSD([subQ0,sQuery(id+"F6.wireOp",EDGE,"E10.0"),sQuery(id+"F6.wireOp",EDGE,"E11"),sQuery(id+"F6.wireOp",EDGE,"E12")])],"isStart":false})]}),makeQuery(id+"F19.opExtrude","CAP_FACE",FACE,{"disambiguationData":[OSD([sQuery(id+"F18.wireOp",EDGE,"E32.left"),sQuery(id+"F18.wireOp",EDGE,"E32.right"),sQuery(id+"F18.wireOp",EDGE,"E33"),sQuery(id+"F18.wireOp",EDGE,"6943048b-c902-4e26-99fd-97bb197fedb8"),sQuery(id+"F18.wireOp",EDGE,"E34"),sQuery(id+"F18.wireOp",EDGE,"E35")])],"isStart":false}),makeQuery(id+"F19.opExtrude","CAP_FACE",FACE,{"disambiguationData":[OSD([sQuery(id+"F18.wireOp",EDGE,"6df5da01-636c-4fa1-a154-6959b493e0280.MirrorCS"),sQuery(id+"F18.wireOp",EDGE,"8fe4f21a-40d9-4eee-a692-7fc8709130e30.MirrorCS"),sQuery(id+"F18.wireOp",EDGE,"7f15d878-ce14-4078-be7b-5ededd66effc0.MirrorCS"),sQuery(id+"F18.wireOp",EDGE,"1ae5cb18-7ae8-489c-8bf4-f5e9a86dfa970.MirrorCS"),sQuery(id+"F18.wireOp",EDGE,"720fc289-6002-463f-9985-f6a57c39472f0.MirrorCS"),sQuery(id+"F18.wireOp",EDGE,"14feacf6-0e8a-4ab1-8ffb-d78e7fce1ae00.MirrorCS")])],"isStart":false})]}),makeQuery(id+"F21.opExtrude","CAP_FACE",FACE,{"disambiguationData":[OSD([sQuery(id+"F20.wireOp",EDGE,"E41"),sQuery(id+"F20.wireOp",EDGE,"E42"),sQuery(id+"F20.wireOp",EDGE,"E43"),sQuery(id+"F20.wireOp",EDGE,"E44"),sQuery(id+"F20.wireOp",EDGE,"E45"),sQuery(id+"F20.wireOp",EDGE,"E46")])],"isStart":false}),makeQuery(id+"F21.opExtrude","CAP_FACE",FACE,{"disambiguationData":[OSD([sQuery(id+"F20.wireOp",EDGE,"E47"),sQuery(id+"F20.wireOp",EDGE,"E48"),sQuery(id+"F20.wireOp",EDGE,"E49"),sQuery(id+"F20.wireOp",EDGE,"E50"),sQuery(id+"F20.wireOp",EDGE,"E51"),sQuery(id+"F20.wireOp",EDGE,"E52")])],"isStart":false}),makeQuery(id+"F21.opExtrude","CAP_FACE",FACE,{"disambiguationData":[OSD([sQuery(id+"F20.wireOp",EDGE,"E53.MirrorCS"),sQuery(id+"F20.wireOp",EDGE,"E54.MirrorCS"),sQuery(id+"F20.wireOp",EDGE,"E55.MirrorCS"),sQuery(id+"F20.wireOp",EDGE,"E56.MirrorCS"),sQuery(id+"F20.wireOp",EDGE,"E57.MirrorCS"),sQuery(id+"F20.wireOp",EDGE,"E58.MirrorCS")])],"isStart":false}),makeQuery(id+"F21.opExtrude","CAP_FACE",FACE,{"disambiguationData":[OSD([sQuery(id+"F20.wireOp",EDGE,"E59.MirrorCS"),sQuery(id+"F20.wireOp",EDGE,"E60.MirrorCS"),sQuery(id+"F20.wireOp",EDGE,"E61.MirrorCS"),sQuery(id+"F20.wireOp",EDGE,"E62.MirrorCS"),sQuery(id+"F20.wireOp",EDGE,"E63.MirrorCS"),sQuery(id+"F20.wireOp",EDGE,"E64.MirrorCS")])],"isStart":false})]});}
            extrude(context, id + "F23", {"entities" : qUnion([Q0]), "operationType" : NewBodyOperationType.REMOVE, "endBound" : BoundingType.UP_TO_SURFACE, "oppositeDirection" : true, "endBoundEntityFace" : qUnion([Q1]), "depth" : 25.4 * mm});
        }
    });
